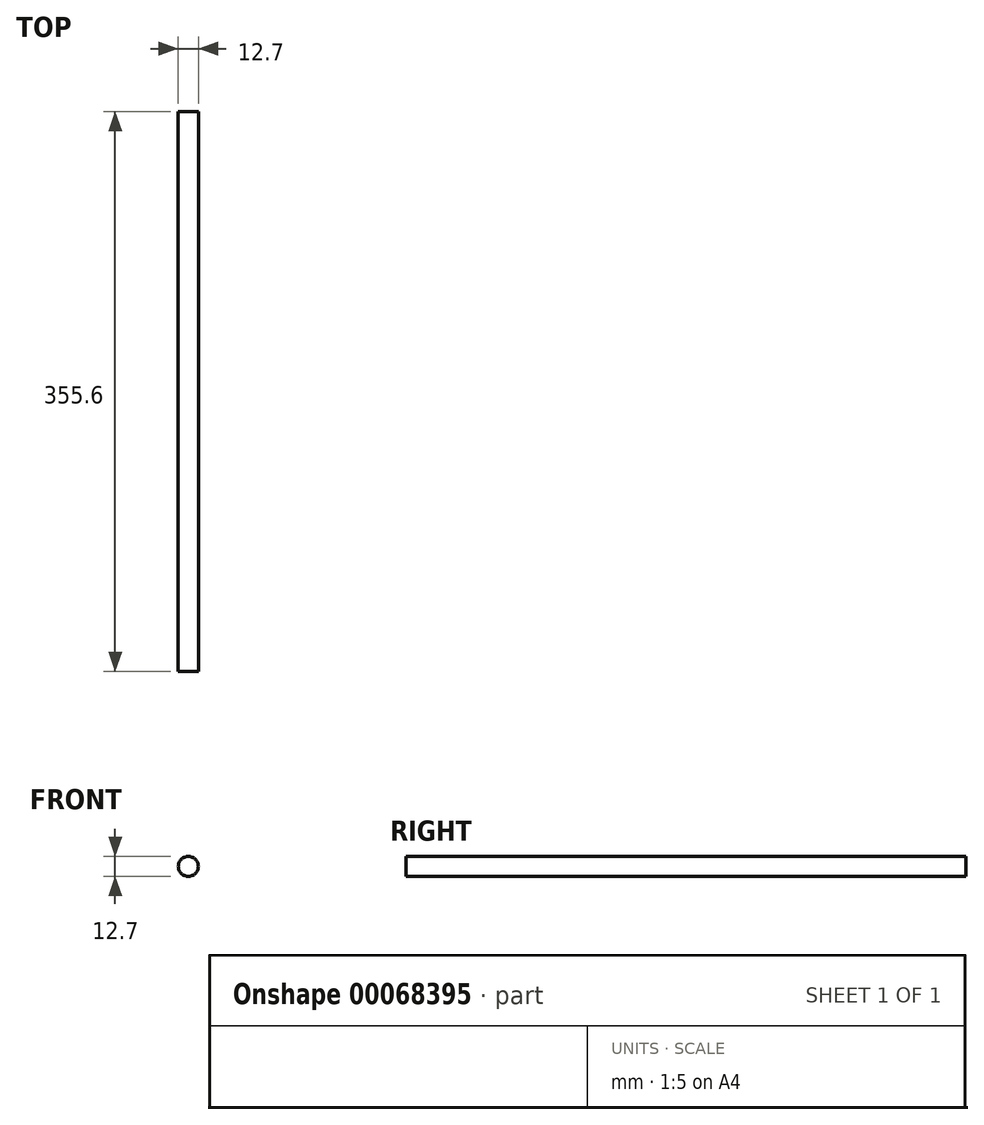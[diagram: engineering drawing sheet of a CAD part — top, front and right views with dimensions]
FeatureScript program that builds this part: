
annotation { "Feature Type Name" : "Feature", "Feature Type Description" : "" }
export const myFeature = defineFeature(function(context is Context, id is Id, definition is map)
    precondition{}
    {
        {
            var Q0;
            Q0=qCreatedBy(makeId("Front.planeOp"),FACE);
            var sketch = newSketch(context, id + "F0", { "sketchPlane" : qUnion([Q0])});
            skCircle(sketch, "E0", {"center": v(0, 0) * mm, "radius": 6.35 * mm});
            skSolve(sketch);
        }
        {
            var Q0;
            Q0=makeQuery(id+"F0.imprint","IMPRINT",FACE,{"disambiguationData":[TD([[makeQuery(id+"F0.imprint","IMPRINT",EDGE,{"derivedFrom":sQuery(id+"F0.wireOp",EDGE,"E0")}),1.0]])]});
            extrude(context, id + "F1", {"entities" : qUnion([Q0]), "depth" : 355.6 * mm});
        }
    });
